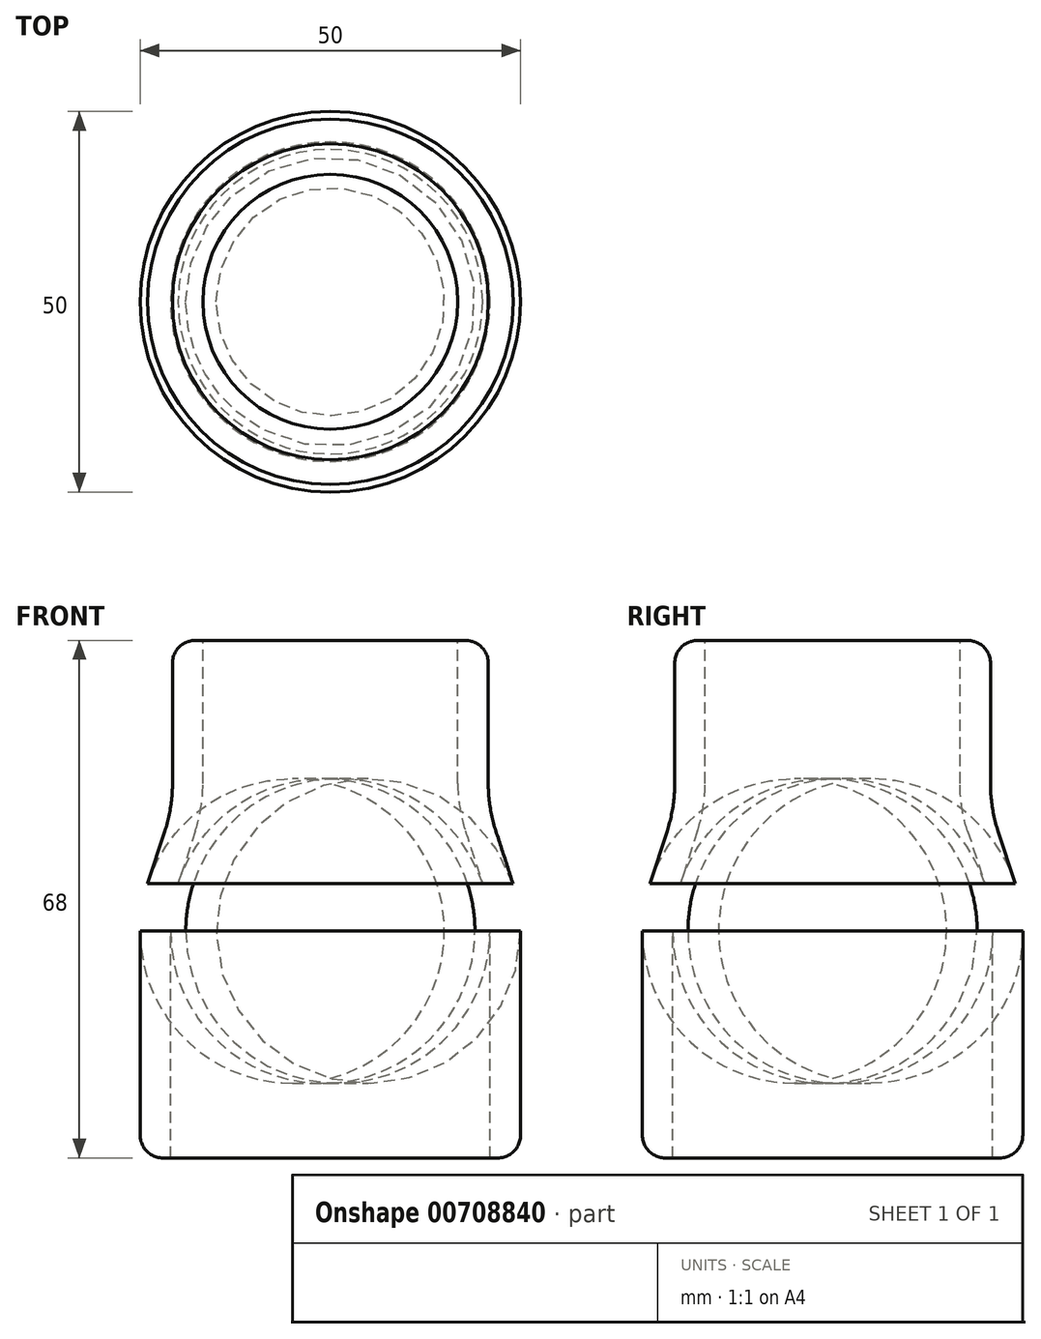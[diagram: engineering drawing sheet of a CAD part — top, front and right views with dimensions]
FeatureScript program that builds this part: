
annotation { "Feature Type Name" : "Feature", "Feature Type Description" : "" }
export const myFeature = defineFeature(function(context is Context, id is Id, definition is map)
    precondition{}
    {
        {
            var Q0;
            Q0=qCreatedBy(makeId("Front.planeOp"),FACE);
            var sketch = newSketch(context, id + "F0", { "sketchPlane" : qUnion([Q0])});
            skLineSegment(sketch, "E0", {"start": v(0, 34.09) * mm, "end": v(0, -33.91) * mm});
            skLineSegment(sketch, "E1", {"start": v(20.75, 34.09) * mm, "end": v(20.75, 15.27) * mm});
            skLineSegment(sketch, "E2", {"start": v(21.74, 9.06) * mm, "end": v(24, 2.12) * mm});
            skLineSegment(sketch, "E3", {"start": v(25, -4.1) * mm, "end": v(25, -33.91) * mm});
            skLineSegment(sketch, "E4", {"start": v(25, -33.91) * mm, "end": v(21, -33.91) * mm});
            skLineSegment(sketch, "E5", {"start": v(21, -33.91) * mm, "end": v(21, -4.1) * mm});
            skLineSegment(sketch, "E6", {"start": v(20, 2.12) * mm, "end": v(17.74, 9.06) * mm});
            skLineSegment(sketch, "E7", {"start": v(16.75, 15.27) * mm, "end": v(16.75, 34.09) * mm});
            skLineSegment(sketch, "E8", {"start": v(16.75, 34.09) * mm, "end": v(20.75, 34.09) * mm});
            skPoint(sketch, "E9.visualSharp", {"position": v(16.75, 12.09) * mm});
            skArc(sketch, "E9.filletArc", {"start": v(16.75, 15.27) * mm, "mid": v(17, 12.13) * mm, "end": v(17.74, 9.06) * mm});
            skPoint(sketch, "E10.visualSharp", {"position": v(21, -0.91) * mm});
            skArc(sketch, "E10.filletArc", {"start": v(21, -4.1) * mm, "mid": v(20.75, -0.95) * mm, "end": v(20, 2.12) * mm});
            skPoint(sketch, "E11.visualSharp", {"position": v(25, -0.91) * mm});
            skArc(sketch, "E11.filletArc", {"start": v(25, -4.1) * mm, "mid": v(24.75, -0.95) * mm, "end": v(24, 2.12) * mm});
            skPoint(sketch, "E12.visualSharp", {"position": v(20.75, 12.09) * mm});
            skArc(sketch, "E12.filletArc", {"start": v(20.75, 15.27) * mm, "mid": v(21, 12.13) * mm, "end": v(21.74, 9.06) * mm});
            skSolve(sketch);
        }
        {
            var Q0;
            Q0=makeQuery(id+"F0.imprint","IMPRINT",FACE,{"disambiguationData":[TD([[makeQuery(id+"F0.imprint","IMPRINT",EDGE,{"derivedFrom":sQuery(id+"F0.wireOp",EDGE,"E1")}),-1.0]])]});
            var Q1;
            Q1=sQuery(id+"F0.wireOp",EDGE,"E0");
            revolve(context, id + "F1", {"surfaceOperationType" : NewSurfaceOperationType.NEW, "entities" : qUnion([Q0]), "axis" : qUnion([Q1]), "revolveType" : RevolveType.FULL});
        }
        {
            var Q0;
            Q0=makeQuery(id+"F1.opRevolve","SWEPT_EDGE",EDGE,{"disambiguationData":[OSD([sQuery(id+"F0.wireOp",EDGE,"E1"),sQuery(id+"F0.wireOp",EDGE,"E8")])]});
            var Q1;
            Q1=makeQuery(id+"F1.opRevolve","SWEPT_EDGE",EDGE,{"disambiguationData":[OSD([sQuery(id+"F0.wireOp",EDGE,"E3"),sQuery(id+"F0.wireOp",EDGE,"E4")])]});
            fillet(context, id + "F2", {"entities" : qUnion([Q0, Q1]), "radius" : 3 * mm, "tangentPropagation" : true, "allowEdgeOverflow" : false});
        }
    });
